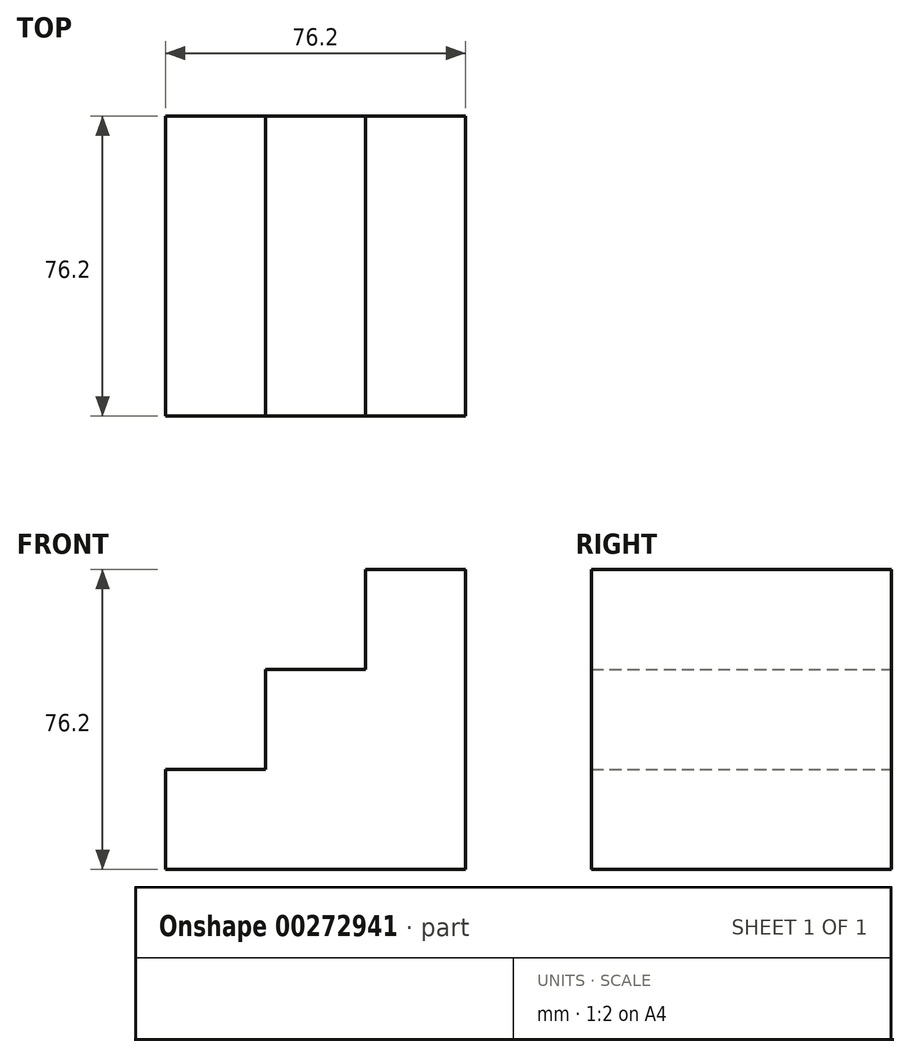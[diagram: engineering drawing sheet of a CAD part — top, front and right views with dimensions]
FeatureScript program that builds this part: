
annotation { "Feature Type Name" : "Feature", "Feature Type Description" : "" }
export const myFeature = defineFeature(function(context is Context, id is Id, definition is map)
    precondition{}
    {
        {
            var Q0;
            Q0=qCreatedBy(makeId("Front.planeOp"),FACE);
            var sketch = newSketch(context, id + "F0", { "sketchPlane" : qUnion([Q0])});
            skLineSegment(sketch, "E0", {"start": v(1.73, 55.77) * mm, "end": v(1.73, -20.43) * mm});
            skLineSegment(sketch, "E1", {"start": v(1.73, -20.43) * mm, "end": v(-74.47, -20.43) * mm});
            skLineSegment(sketch, "E2", {"start": v(-74.47, -20.43) * mm, "end": v(-74.47, 4.97) * mm});
            skLineSegment(sketch, "E3", {"start": v(-74.47, 4.97) * mm, "end": v(-49.07, 4.97) * mm});
            skLineSegment(sketch, "E4", {"start": v(-49.07, 4.97) * mm, "end": v(-49.07, 30.37) * mm});
            skLineSegment(sketch, "E5", {"start": v(-49.07, 30.37) * mm, "end": v(-23.67, 30.37) * mm});
            skLineSegment(sketch, "E6", {"start": v(-23.67, 30.37) * mm, "end": v(-23.67, 55.77) * mm});
            skLineSegment(sketch, "E7", {"start": v(-23.67, 55.77) * mm, "end": v(1.73, 55.77) * mm});
            skSolve(sketch);
        }
        {
            var Q0;
            Q0 = qSketchRegion(id + "F0", true);
            extrude(context, id + "F1", {"entities" : qUnion([Q0]), "depth" : 76.2 * mm});
        }
    });
